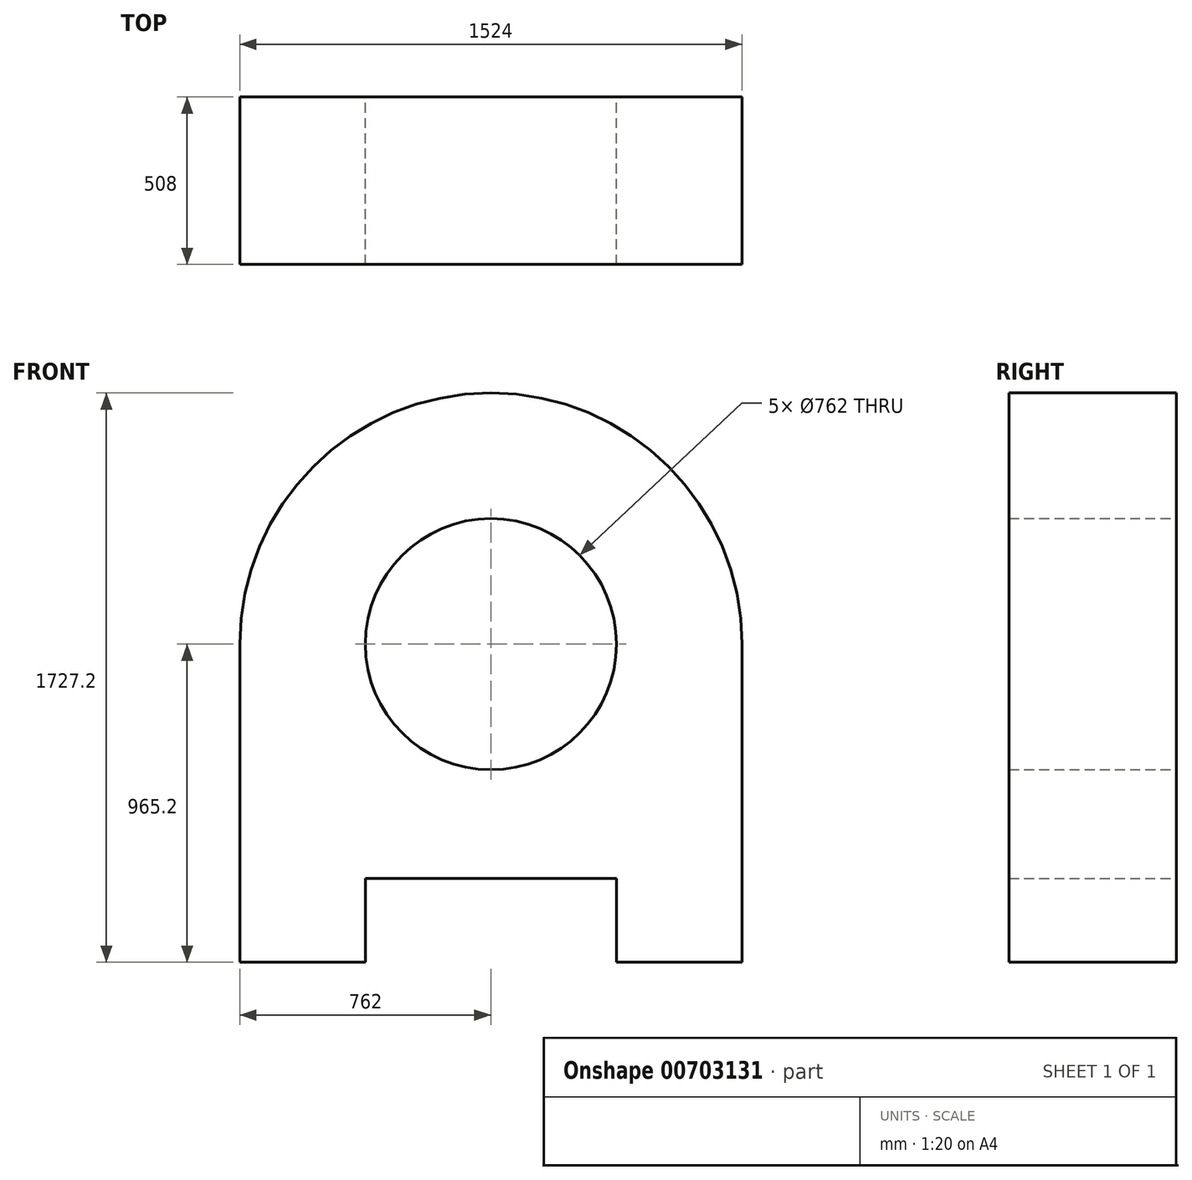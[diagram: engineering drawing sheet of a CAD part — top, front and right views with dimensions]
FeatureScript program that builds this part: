
annotation { "Feature Type Name" : "Feature", "Feature Type Description" : "" }
export const myFeature = defineFeature(function(context is Context, id is Id, definition is map)
    precondition{}
    {
        {
            var Q0;
            Q0=qCreatedBy(makeId("Front.planeOp"),FACE);
            var sketch = newSketch(context, id + "F0", { "sketchPlane" : qUnion([Q0])});
            skLineSegment(sketch, "E0.top", {"start": v(762, -482.6) * mm, "end": v(381, -482.6) * mm});
            skLineSegment(sketch, "E0.left", {"start": v(762, 482.6) * mm, "end": v(762, -482.6) * mm});
            skLineSegment(sketch, "E0.right", {"start": v(-762, 482.6) * mm, "end": v(-762, -482.6) * mm});
            skPoint(sketch, "E0.middle", {"position": v(0, 0) * mm});
            skLineSegment(sketch, "E1", {"start": v(-381, -482.6) * mm, "end": v(-381, -228.6) * mm});
            skLineSegment(sketch, "E2", {"start": v(-381, -228.6) * mm, "end": v(381, -228.6) * mm});
            skLineSegment(sketch, "E3", {"start": v(381, -228.6) * mm, "end": v(381, -482.6) * mm});
            skLineSegment(sketch, "E4.trimOffspring", {"start": v(-381, -482.6) * mm, "end": v(-762, -482.6) * mm});
            skArc(sketch, "E5", {"start": v(762, 482.6) * mm, "mid": v(0, 1244.6) * mm, "end": v(-762, 482.6) * mm});
            skCircle(sketch, "E6", {"center": v(0, 482.6) * mm, "radius": 381 * mm});
            skSolve(sketch);
        }
        {
            var Q0;
            {var subQ0=sQuery(id+"F0.wireOp",EDGE,"E5");Q0=makeQuery(id+"F0.imprint","IMPRINT",FACE,{"disambiguationData":[TD([[makeQuery(id+"F0.imprint","IMPRINT",EDGE,{"derivedFrom":subQ0}),1.0]])]});}
            var Q1;
            Q1=makeQuery(id+"F0.imprint","IMPRINT",FACE,{"disambiguationData":[TD([[makeQuery(id+"F0.imprint","IMPRINT",EDGE,{"derivedFrom":sQuery(id+"F0.wireOp",EDGE,"E0.top")}),-1.0]])]});
            extrude(context, id + "F1", {"entities" : qUnion([Q0, Q1]), "depth" : 508 * mm, "offsetDistance" : 25.4 * mm});
        }
    });
